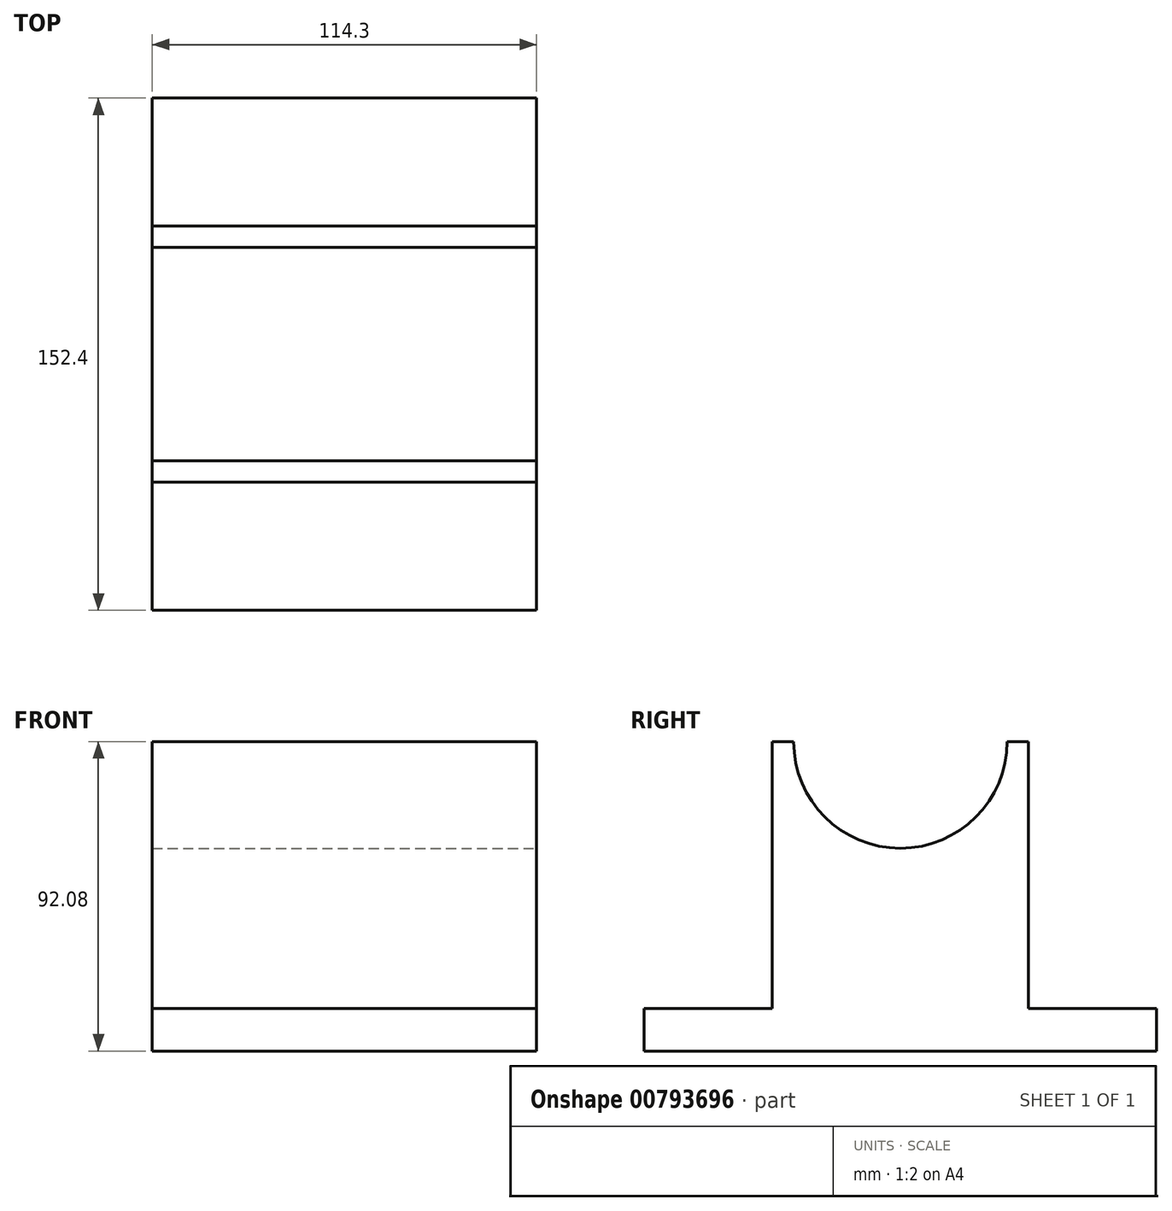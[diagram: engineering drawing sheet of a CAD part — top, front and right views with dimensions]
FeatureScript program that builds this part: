
annotation { "Feature Type Name" : "Feature", "Feature Type Description" : "" }
export const myFeature = defineFeature(function(context is Context, id is Id, definition is map)
    precondition{}
    {
        {
            var Q0;
            Q0=qCreatedBy(makeId("Right.planeOp"),FACE);
            var sketch = newSketch(context, id + "F0", { "sketchPlane" : qUnion([Q0])});
            skLineSegment(sketch, "E0", {"start": v(0, 0) * mm, "end": v(152.4, 0) * mm});
            skLineSegment(sketch, "E1", {"start": v(0, 0) * mm, "end": v(0, 12.7) * mm});
            skLineSegment(sketch, "E2", {"start": v(0, 12.7) * mm, "end": v(38.1, 12.7) * mm});
            skLineSegment(sketch, "E3", {"start": v(152.4, 0) * mm, "end": v(152.4, 12.7) * mm});
            skLineSegment(sketch, "E4", {"start": v(152.4, 12.7) * mm, "end": v(114.3, 12.7) * mm});
            skLineSegment(sketch, "E5", {"start": v(38.1, 12.7) * mm, "end": v(38.1, 92.07) * mm});
            skLineSegment(sketch, "E6", {"start": v(114.3, 12.7) * mm, "end": v(114.3, 92.07) * mm});
            skLineSegment(sketch, "E7", {"start": v(114.3, 92.07) * mm, "end": v(38.1, 92.07) * mm});
            skSolve(sketch);
        }
        {
            var Q0;
            Q0 = qSketchRegion(id + "F0", true);
            extrude(context, id + "F1", {"entities" : qUnion([Q0]), "depth" : 114.3 * mm, "offsetDistance" : 25.4 * mm});
        }
        {
            var Q0;
            Q0=makeQuery(id+"F1.opExtrude","CAP_FACE",FACE,{"disambiguationData":[OSD([sQuery(id+"F0.wireOp",EDGE,"E0"),sQuery(id+"F0.wireOp",EDGE,"E1"),sQuery(id+"F0.wireOp",EDGE,"E2"),sQuery(id+"F0.wireOp",EDGE,"E3"),sQuery(id+"F0.wireOp",EDGE,"E4"),sQuery(id+"F0.wireOp",EDGE,"E5"),sQuery(id+"F0.wireOp",EDGE,"E6"),sQuery(id+"F0.wireOp",EDGE,"E7")])],"isStart":false});
            var sketch = newSketch(context, id + "F2", { "sketchPlane" : qUnion([Q0])});
            skCircle(sketch, "E8", {"center": v(76.2, 92.07) * mm, "radius": 31.75 * mm});
            skSolve(sketch);
        }
        {
            var Q0;
            {var subQ0=sQuery(id+"F2.wireOp",EDGE,"E8");var subQ1=makeQuery(id+"F1.opExtrude","CAP_EDGE",EDGE,{"disambiguationData":[OSD([sQuery(id+"F0.wireOp",EDGE,"E7")])],"isStart":false});var subQ2=makeQuery(id+"F2.imprint","INTERSECT",VERTEX,{"disambiguationData":[OD(0.0)],"derivedFrom":[subQ1,subQ0]});Q0=makeQuery(id+"F2.imprint","IMPRINT",FACE,{"disambiguationData":[TD([[makeQuery(id+"F2.imprint","IMPRINT",EDGE,{"disambiguationData":[TD([[subQ2,-1.0]])],"derivedFrom":subQ0}),1.0]])]});}
            extrude(context, id + "F3", {"entities" : qUnion([Q0]), "operationType" : NewBodyOperationType.REMOVE, "endBound" : BoundingType.THROUGH_ALL, "oppositeDirection" : true, "depth" : 25.4 * mm, "offsetDistance" : 25.4 * mm});
        }
    });
